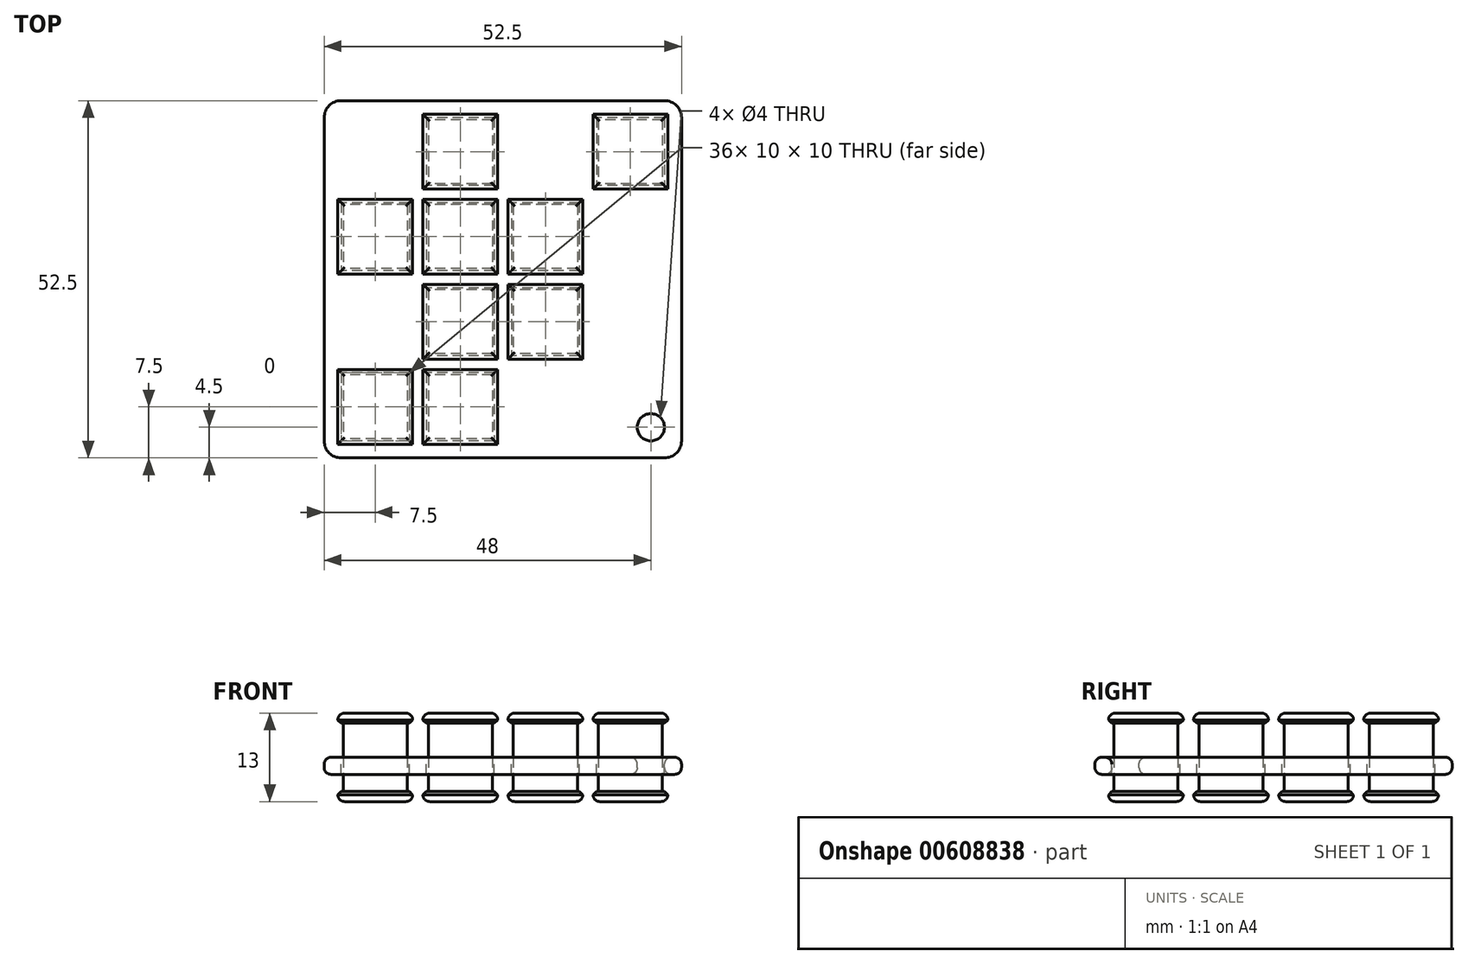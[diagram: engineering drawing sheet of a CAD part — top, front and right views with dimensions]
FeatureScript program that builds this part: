
annotation { "Feature Type Name" : "Feature", "Feature Type Description" : "" }
export const myFeature = defineFeature(function(context is Context, id is Id, definition is map)
    precondition{}
    {
        {
            var Q0;
            Q0=qCreatedBy(makeId("Top.planeOp"),FACE);
            var sketch = newSketch(context, id + "F0", { "sketchPlane" : qUnion([Q0])});
            skLineSegment(sketch, "E0.bottom", {"start": v(5, 5) * mm, "end": v(-5, 5) * mm});
            skLineSegment(sketch, "E0.top", {"start": v(5, -5) * mm, "end": v(-5, -5) * mm});
            skLineSegment(sketch, "E0.left", {"start": v(5, 5) * mm, "end": v(5, -5) * mm});
            skLineSegment(sketch, "E0.right", {"start": v(-5, 5) * mm, "end": v(-5, -5) * mm});
            skPoint(sketch, "E0.middle", {"position": v(0, 0) * mm});
            skLineSegment(sketch, "E1.0.2.0", {"start": v(5, 30) * mm, "end": v(-5, 30) * mm});
            skLineSegment(sketch, "E1.0.2.1", {"start": v(5, 30) * mm, "end": v(5, 20) * mm});
            skLineSegment(sketch, "E1.0.2.2", {"start": v(5, 20) * mm, "end": v(-5, 20) * mm});
            skLineSegment(sketch, "E1.0.2.3", {"start": v(-5, 30) * mm, "end": v(-5, 20) * mm});
            skLineSegment(sketch, "E1.1.0.0", {"start": v(17.5, 5) * mm, "end": v(7.5, 5) * mm});
            skLineSegment(sketch, "E1.1.0.1", {"start": v(17.5, 5) * mm, "end": v(17.5, -5) * mm});
            skLineSegment(sketch, "E1.1.0.2", {"start": v(17.5, -5) * mm, "end": v(7.5, -5) * mm});
            skLineSegment(sketch, "E1.1.0.3", {"start": v(7.5, 5) * mm, "end": v(7.5, -5) * mm});
            skLineSegment(sketch, "E1.1.1.0", {"start": v(17.5, 17.5) * mm, "end": v(7.5, 17.5) * mm});
            skLineSegment(sketch, "E1.1.1.1", {"start": v(17.5, 17.5) * mm, "end": v(17.5, 7.5) * mm});
            skLineSegment(sketch, "E1.1.1.2", {"start": v(17.5, 7.5) * mm, "end": v(7.5, 7.5) * mm});
            skLineSegment(sketch, "E1.1.1.3", {"start": v(7.5, 17.5) * mm, "end": v(7.5, 7.5) * mm});
            skLineSegment(sketch, "E1.1.2.0", {"start": v(17.5, 30) * mm, "end": v(7.5, 30) * mm});
            skLineSegment(sketch, "E1.1.2.1", {"start": v(17.5, 30) * mm, "end": v(17.5, 20) * mm});
            skLineSegment(sketch, "E1.1.2.2", {"start": v(17.5, 20) * mm, "end": v(7.5, 20) * mm});
            skLineSegment(sketch, "E1.1.2.3", {"start": v(7.5, 30) * mm, "end": v(7.5, 20) * mm});
            skLineSegment(sketch, "E1.1.3.0", {"start": v(17.5, 42.5) * mm, "end": v(7.5, 42.5) * mm});
            skLineSegment(sketch, "E1.1.3.1", {"start": v(17.5, 42.5) * mm, "end": v(17.5, 32.5) * mm});
            skLineSegment(sketch, "E1.1.3.2", {"start": v(17.5, 32.5) * mm, "end": v(7.5, 32.5) * mm});
            skLineSegment(sketch, "E1.1.3.3", {"start": v(7.5, 42.5) * mm, "end": v(7.5, 32.5) * mm});
            skLineSegment(sketch, "E1.2.1.0", {"start": v(30, 17.5) * mm, "end": v(20, 17.5) * mm});
            skLineSegment(sketch, "E1.2.1.1", {"start": v(30, 17.5) * mm, "end": v(30, 7.5) * mm});
            skLineSegment(sketch, "E1.2.1.2", {"start": v(30, 7.5) * mm, "end": v(20, 7.5) * mm});
            skLineSegment(sketch, "E1.2.1.3", {"start": v(20, 17.5) * mm, "end": v(20, 7.5) * mm});
            skLineSegment(sketch, "E1.2.2.0", {"start": v(30, 30) * mm, "end": v(20, 30) * mm});
            skLineSegment(sketch, "E1.2.2.1", {"start": v(30, 30) * mm, "end": v(30, 20) * mm});
            skLineSegment(sketch, "E1.2.2.2", {"start": v(30, 20) * mm, "end": v(20, 20) * mm});
            skLineSegment(sketch, "E1.2.2.3", {"start": v(20, 30) * mm, "end": v(20, 20) * mm});
            skLineSegment(sketch, "E1.3.3.0", {"start": v(42.5, 42.5) * mm, "end": v(32.5, 42.5) * mm});
            skLineSegment(sketch, "E1.3.3.1", {"start": v(42.5, 42.5) * mm, "end": v(42.5, 32.5) * mm});
            skLineSegment(sketch, "E1.3.3.2", {"start": v(42.5, 32.5) * mm, "end": v(32.5, 32.5) * mm});
            skLineSegment(sketch, "E1.3.3.3", {"start": v(32.5, 42.5) * mm, "end": v(32.5, 32.5) * mm});
            skLineSegment(sketch, "E2.bottom", {"start": v(-5, -7.5) * mm, "end": v(42.5, -7.5) * mm});
            skLineSegment(sketch, "E2.top", {"start": v(-5, 45) * mm, "end": v(42.5, 45) * mm});
            skLineSegment(sketch, "E2.left", {"start": v(-7.5, -5) * mm, "end": v(-7.5, 42.5) * mm});
            skLineSegment(sketch, "E2.right", {"start": v(45, -5) * mm, "end": v(45, 42.5) * mm});
            skPoint(sketch, "E3.visualSharp", {"position": v(-7.5, 45) * mm});
            skArc(sketch, "E3.filletArc", {"start": v(-5, 45) * mm, "mid": v(-6.77, 44.27) * mm, "end": v(-7.5, 42.5) * mm});
            skPoint(sketch, "E4.visualSharp", {"position": v(-7.5, -7.5) * mm});
            skArc(sketch, "E4.filletArc", {"start": v(-7.5, -5) * mm, "mid": v(-6.77, -6.77) * mm, "end": v(-5, -7.5) * mm});
            skPoint(sketch, "E5.visualSharp", {"position": v(45, -7.5) * mm});
            skArc(sketch, "E5.filletArc", {"start": v(42.5, -7.5) * mm, "mid": v(44.27, -6.77) * mm, "end": v(45, -5) * mm});
            skPoint(sketch, "E6.visualSharp", {"position": v(45, 45) * mm});
            skArc(sketch, "E6.filletArc", {"start": v(45, 42.5) * mm, "mid": v(44.27, 44.27) * mm, "end": v(42.5, 45) * mm});
            skLineSegment(sketch, "E7.0", {"start": v(4.7, 4.7) * mm, "end": v(-4.7, 4.7) * mm});
            skLineSegment(sketch, "E7.1", {"start": v(4.7, 4.7) * mm, "end": v(4.7, -4.7) * mm});
            skLineSegment(sketch, "E7.2", {"start": v(4.7, -4.7) * mm, "end": v(-4.7, -4.7) * mm});
            skLineSegment(sketch, "E7.3", {"start": v(-4.7, 4.7) * mm, "end": v(-4.7, -4.7) * mm});
            skLineSegment(sketch, "E8.0.2.0", {"start": v(4.7, 29.7) * mm, "end": v(-4.7, 29.7) * mm});
            skLineSegment(sketch, "E8.0.2.1", {"start": v(4.7, 29.7) * mm, "end": v(4.7, 20.3) * mm});
            skLineSegment(sketch, "E8.0.2.2", {"start": v(4.7, 20.3) * mm, "end": v(-4.7, 20.3) * mm});
            skLineSegment(sketch, "E8.0.2.3", {"start": v(-4.7, 29.7) * mm, "end": v(-4.7, 20.3) * mm});
            skLineSegment(sketch, "E8.1.0.0", {"start": v(17.2, 4.7) * mm, "end": v(7.8, 4.7) * mm});
            skLineSegment(sketch, "E8.1.0.1", {"start": v(17.2, 4.7) * mm, "end": v(17.2, -4.7) * mm});
            skLineSegment(sketch, "E8.1.0.2", {"start": v(17.2, -4.7) * mm, "end": v(7.8, -4.7) * mm});
            skLineSegment(sketch, "E8.1.0.3", {"start": v(7.8, 4.7) * mm, "end": v(7.8, -4.7) * mm});
            skLineSegment(sketch, "E8.1.1.0", {"start": v(17.2, 17.2) * mm, "end": v(7.8, 17.2) * mm});
            skLineSegment(sketch, "E8.1.1.1", {"start": v(17.2, 17.2) * mm, "end": v(17.2, 7.8) * mm});
            skLineSegment(sketch, "E8.1.1.2", {"start": v(17.2, 7.8) * mm, "end": v(7.8, 7.8) * mm});
            skLineSegment(sketch, "E8.1.1.3", {"start": v(7.8, 17.2) * mm, "end": v(7.8, 7.8) * mm});
            skLineSegment(sketch, "E8.1.2.0", {"start": v(17.2, 29.7) * mm, "end": v(7.8, 29.7) * mm});
            skLineSegment(sketch, "E8.1.2.1", {"start": v(17.2, 29.7) * mm, "end": v(17.2, 20.3) * mm});
            skLineSegment(sketch, "E8.1.2.2", {"start": v(17.2, 20.3) * mm, "end": v(7.8, 20.3) * mm});
            skLineSegment(sketch, "E8.1.2.3", {"start": v(7.8, 29.7) * mm, "end": v(7.8, 20.3) * mm});
            skLineSegment(sketch, "E8.1.3.0", {"start": v(17.2, 42.2) * mm, "end": v(7.8, 42.2) * mm});
            skLineSegment(sketch, "E8.1.3.1", {"start": v(17.2, 42.2) * mm, "end": v(17.2, 32.8) * mm});
            skLineSegment(sketch, "E8.1.3.2", {"start": v(17.2, 32.8) * mm, "end": v(7.8, 32.8) * mm});
            skLineSegment(sketch, "E8.1.3.3", {"start": v(7.8, 42.2) * mm, "end": v(7.8, 32.8) * mm});
            skLineSegment(sketch, "E8.2.1.0", {"start": v(29.7, 17.2) * mm, "end": v(20.3, 17.2) * mm});
            skLineSegment(sketch, "E8.2.1.1", {"start": v(29.7, 17.2) * mm, "end": v(29.7, 7.8) * mm});
            skLineSegment(sketch, "E8.2.1.2", {"start": v(29.7, 7.8) * mm, "end": v(20.3, 7.8) * mm});
            skLineSegment(sketch, "E8.2.1.3", {"start": v(20.3, 17.2) * mm, "end": v(20.3, 7.8) * mm});
            skLineSegment(sketch, "E8.2.2.0", {"start": v(29.7, 29.7) * mm, "end": v(20.3, 29.7) * mm});
            skLineSegment(sketch, "E8.2.2.1", {"start": v(29.7, 29.7) * mm, "end": v(29.7, 20.3) * mm});
            skLineSegment(sketch, "E8.2.2.2", {"start": v(29.7, 20.3) * mm, "end": v(20.3, 20.3) * mm});
            skLineSegment(sketch, "E8.2.2.3", {"start": v(20.3, 29.7) * mm, "end": v(20.3, 20.3) * mm});
            skLineSegment(sketch, "E8.3.3.0", {"start": v(42.2, 42.2) * mm, "end": v(32.8, 42.2) * mm});
            skLineSegment(sketch, "E8.3.3.1", {"start": v(42.2, 42.2) * mm, "end": v(42.2, 32.8) * mm});
            skLineSegment(sketch, "E8.3.3.2", {"start": v(42.2, 32.8) * mm, "end": v(32.8, 32.8) * mm});
            skLineSegment(sketch, "E8.3.3.3", {"start": v(32.8, 42.2) * mm, "end": v(32.8, 32.8) * mm});
            skLineSegment(sketch, "E8.direction1", {"start": v(-4.7, 4.7) * mm, "end": v(7.8, 4.7) * mm, "construction": true});
            skCircle(sketch, "E9", {"center": v(40.5, -3) * mm, "radius": 2 * mm});
            skSolve(sketch);
        }
        {
            var Q0;
            Q0=makeQuery(id+"F0.imprint","IMPRINT",FACE,{"disambiguationData":[TD([[makeQuery(id+"F0.imprint","IMPRINT",EDGE,{"derivedFrom":sQuery(id+"F0.wireOp",EDGE,"E7.0")}),1.0]])]});
            var Q1;
            Q1=makeQuery(id+"F0.imprint","IMPRINT",FACE,{"disambiguationData":[TD([[makeQuery(id+"F0.imprint","IMPRINT",EDGE,{"derivedFrom":sQuery(id+"F0.wireOp",EDGE,"E8.1.0.0")}),1.0]])]});
            var Q2;
            Q2=makeQuery(id+"F0.imprint","IMPRINT",FACE,{"disambiguationData":[TD([[makeQuery(id+"F0.imprint","IMPRINT",EDGE,{"derivedFrom":sQuery(id+"F0.wireOp",EDGE,"E8.1.1.0")}),1.0]])]});
            var Q3;
            Q3=makeQuery(id+"F0.imprint","IMPRINT",FACE,{"disambiguationData":[TD([[makeQuery(id+"F0.imprint","IMPRINT",EDGE,{"derivedFrom":sQuery(id+"F0.wireOp",EDGE,"E8.2.1.0")}),1.0]])]});
            var Q4;
            Q4=makeQuery(id+"F0.imprint","IMPRINT",FACE,{"disambiguationData":[TD([[makeQuery(id+"F0.imprint","IMPRINT",EDGE,{"derivedFrom":sQuery(id+"F0.wireOp",EDGE,"E8.2.2.0")}),1.0]])]});
            var Q5;
            Q5=makeQuery(id+"F0.imprint","IMPRINT",FACE,{"disambiguationData":[TD([[makeQuery(id+"F0.imprint","IMPRINT",EDGE,{"derivedFrom":sQuery(id+"F0.wireOp",EDGE,"E8.1.2.0")}),1.0]])]});
            var Q6;
            Q6=makeQuery(id+"F0.imprint","IMPRINT",FACE,{"disambiguationData":[TD([[makeQuery(id+"F0.imprint","IMPRINT",EDGE,{"derivedFrom":sQuery(id+"F0.wireOp",EDGE,"E8.0.2.0")}),1.0]])]});
            var Q7;
            Q7=makeQuery(id+"F0.imprint","IMPRINT",FACE,{"disambiguationData":[TD([[makeQuery(id+"F0.imprint","IMPRINT",EDGE,{"derivedFrom":sQuery(id+"F0.wireOp",EDGE,"E8.3.3.0")}),1.0]])]});
            var Q8;
            Q8=makeQuery(id+"F0.imprint","IMPRINT",FACE,{"disambiguationData":[TD([[makeQuery(id+"F0.imprint","IMPRINT",EDGE,{"derivedFrom":sQuery(id+"F0.wireOp",EDGE,"E8.1.3.0")}),1.0]])]});
            extrude(context, id + "F1", {"entities" : qUnion([Q0, Q1, Q2, Q3, Q4, Q5, Q6, Q7, Q8]), "endBound" : BoundingType.SYMMETRIC, "depth" : 10 * mm, "offsetDistance" : 25 * mm});
        }
        {
            var Q0;
            Q0=makeQuery(id+"F0.imprint","IMPRINT",FACE,{"disambiguationData":[TD([[makeQuery(id+"F0.imprint","IMPRINT",EDGE,{"derivedFrom":sQuery(id+"F0.wireOp",EDGE,"E0.bottom")}),-1.0]])]});
            extrude(context, id + "F2", {"entities" : qUnion([Q0]), "oppositeDirection" : true, "depth" : 2.5 * mm, "offsetDistance" : 25 * mm});
        }
        {
            var Q0;
            Q0=makeQuery(id+"F1.opExtrude","CAP_FACE",FACE,{"disambiguationData":[OSD([sQuery(id+"F0.wireOp",EDGE,"E7.0"),sQuery(id+"F0.wireOp",EDGE,"E7.1"),sQuery(id+"F0.wireOp",EDGE,"E7.2"),sQuery(id+"F0.wireOp",EDGE,"E7.3")])],"isStart":false});
            var sketch = newSketch(context, id + "F3", { "sketchPlane" : qUnion([Q0])});
            skLineSegment(sketch, "E10.0", {"start": v(5.5, 5.5) * mm, "end": v(-5.5, 5.5) * mm});
            skLineSegment(sketch, "E10.1", {"start": v(5.5, 5.5) * mm, "end": v(5.5, -5.5) * mm});
            skLineSegment(sketch, "E10.2", {"start": v(5.5, -5.5) * mm, "end": v(-5.5, -5.5) * mm});
            skLineSegment(sketch, "E10.3", {"start": v(-5.5, 5.5) * mm, "end": v(-5.5, -5.5) * mm});
            skLineSegment(sketch, "E11.0.1.0", {"start": v(5.5, 18) * mm, "end": v(-5.5, 18) * mm});
            skLineSegment(sketch, "E11.0.1.1", {"start": v(5.5, 18) * mm, "end": v(5.5, 7) * mm});
            skLineSegment(sketch, "E11.0.1.2", {"start": v(5.5, 7) * mm, "end": v(-5.5, 7) * mm});
            skLineSegment(sketch, "E11.0.1.3", {"start": v(-5.5, 18) * mm, "end": v(-5.5, 7) * mm});
            skLineSegment(sketch, "E11.0.2.0", {"start": v(5.5, 30.5) * mm, "end": v(-5.5, 30.5) * mm});
            skLineSegment(sketch, "E11.0.2.1", {"start": v(5.5, 30.5) * mm, "end": v(5.5, 19.5) * mm});
            skLineSegment(sketch, "E11.0.2.2", {"start": v(5.5, 19.5) * mm, "end": v(-5.5, 19.5) * mm});
            skLineSegment(sketch, "E11.0.2.3", {"start": v(-5.5, 30.5) * mm, "end": v(-5.5, 19.5) * mm});
            skLineSegment(sketch, "E11.0.3.0", {"start": v(5.5, 43) * mm, "end": v(-5.5, 43) * mm});
            skLineSegment(sketch, "E11.0.3.1", {"start": v(5.5, 43) * mm, "end": v(5.5, 32) * mm});
            skLineSegment(sketch, "E11.0.3.2", {"start": v(5.5, 32) * mm, "end": v(-5.5, 32) * mm});
            skLineSegment(sketch, "E11.0.3.3", {"start": v(-5.5, 43) * mm, "end": v(-5.5, 32) * mm});
            skLineSegment(sketch, "E11.1.0.0", {"start": v(18, 5.5) * mm, "end": v(7, 5.5) * mm});
            skLineSegment(sketch, "E11.1.0.1", {"start": v(18, 5.5) * mm, "end": v(18, -5.5) * mm});
            skLineSegment(sketch, "E11.1.0.2", {"start": v(18, -5.5) * mm, "end": v(7, -5.5) * mm});
            skLineSegment(sketch, "E11.1.0.3", {"start": v(7, 5.5) * mm, "end": v(7, -5.5) * mm});
            skLineSegment(sketch, "E11.1.1.0", {"start": v(18, 18) * mm, "end": v(7, 18) * mm});
            skLineSegment(sketch, "E11.1.1.1", {"start": v(18, 18) * mm, "end": v(18, 7) * mm});
            skLineSegment(sketch, "E11.1.1.2", {"start": v(18, 7) * mm, "end": v(7, 7) * mm});
            skLineSegment(sketch, "E11.1.1.3", {"start": v(7, 18) * mm, "end": v(7, 7) * mm});
            skLineSegment(sketch, "E11.1.2.0", {"start": v(18, 30.5) * mm, "end": v(7, 30.5) * mm});
            skLineSegment(sketch, "E11.1.2.1", {"start": v(18, 30.5) * mm, "end": v(18, 19.5) * mm});
            skLineSegment(sketch, "E11.1.2.2", {"start": v(18, 19.5) * mm, "end": v(7, 19.5) * mm});
            skLineSegment(sketch, "E11.1.2.3", {"start": v(7, 30.5) * mm, "end": v(7, 19.5) * mm});
            skLineSegment(sketch, "E11.1.3.0", {"start": v(18, 43) * mm, "end": v(7, 43) * mm});
            skLineSegment(sketch, "E11.1.3.1", {"start": v(18, 43) * mm, "end": v(18, 32) * mm});
            skLineSegment(sketch, "E11.1.3.2", {"start": v(18, 32) * mm, "end": v(7, 32) * mm});
            skLineSegment(sketch, "E11.1.3.3", {"start": v(7, 43) * mm, "end": v(7, 32) * mm});
            skLineSegment(sketch, "E11.2.0.0", {"start": v(30.5, 5.5) * mm, "end": v(19.5, 5.5) * mm});
            skLineSegment(sketch, "E11.2.0.1", {"start": v(30.5, 5.5) * mm, "end": v(30.5, -5.5) * mm});
            skLineSegment(sketch, "E11.2.0.2", {"start": v(30.5, -5.5) * mm, "end": v(19.5, -5.5) * mm});
            skLineSegment(sketch, "E11.2.0.3", {"start": v(19.5, 5.5) * mm, "end": v(19.5, -5.5) * mm});
            skLineSegment(sketch, "E11.2.1.0", {"start": v(30.5, 18) * mm, "end": v(19.5, 18) * mm});
            skLineSegment(sketch, "E11.2.1.1", {"start": v(30.5, 18) * mm, "end": v(30.5, 7) * mm});
            skLineSegment(sketch, "E11.2.1.2", {"start": v(30.5, 7) * mm, "end": v(19.5, 7) * mm});
            skLineSegment(sketch, "E11.2.1.3", {"start": v(19.5, 18) * mm, "end": v(19.5, 7) * mm});
            skLineSegment(sketch, "E11.2.2.0", {"start": v(30.5, 30.5) * mm, "end": v(19.5, 30.5) * mm});
            skLineSegment(sketch, "E11.2.2.1", {"start": v(30.5, 30.5) * mm, "end": v(30.5, 19.5) * mm});
            skLineSegment(sketch, "E11.2.2.2", {"start": v(30.5, 19.5) * mm, "end": v(19.5, 19.5) * mm});
            skLineSegment(sketch, "E11.2.2.3", {"start": v(19.5, 30.5) * mm, "end": v(19.5, 19.5) * mm});
            skLineSegment(sketch, "E11.2.3.0", {"start": v(30.5, 43) * mm, "end": v(19.5, 43) * mm});
            skLineSegment(sketch, "E11.2.3.1", {"start": v(30.5, 43) * mm, "end": v(30.5, 32) * mm});
            skLineSegment(sketch, "E11.2.3.2", {"start": v(30.5, 32) * mm, "end": v(19.5, 32) * mm});
            skLineSegment(sketch, "E11.2.3.3", {"start": v(19.5, 43) * mm, "end": v(19.5, 32) * mm});
            skLineSegment(sketch, "E11.3.0.0", {"start": v(43, 5.5) * mm, "end": v(32, 5.5) * mm});
            skLineSegment(sketch, "E11.3.0.1", {"start": v(43, 5.5) * mm, "end": v(43, -5.5) * mm});
            skLineSegment(sketch, "E11.3.0.2", {"start": v(43, -5.5) * mm, "end": v(32, -5.5) * mm});
            skLineSegment(sketch, "E11.3.0.3", {"start": v(32, 5.5) * mm, "end": v(32, -5.5) * mm});
            skLineSegment(sketch, "E11.3.1.0", {"start": v(43, 18) * mm, "end": v(32, 18) * mm});
            skLineSegment(sketch, "E11.3.1.1", {"start": v(43, 18) * mm, "end": v(43, 7) * mm});
            skLineSegment(sketch, "E11.3.1.2", {"start": v(43, 7) * mm, "end": v(32, 7) * mm});
            skLineSegment(sketch, "E11.3.1.3", {"start": v(32, 18) * mm, "end": v(32, 7) * mm});
            skLineSegment(sketch, "E11.3.2.0", {"start": v(43, 30.5) * mm, "end": v(32, 30.5) * mm});
            skLineSegment(sketch, "E11.3.2.1", {"start": v(43, 30.5) * mm, "end": v(43, 19.5) * mm});
            skLineSegment(sketch, "E11.3.2.2", {"start": v(43, 19.5) * mm, "end": v(32, 19.5) * mm});
            skLineSegment(sketch, "E11.3.2.3", {"start": v(32, 30.5) * mm, "end": v(32, 19.5) * mm});
            skLineSegment(sketch, "E11.3.3.0", {"start": v(43, 43) * mm, "end": v(32, 43) * mm});
            skLineSegment(sketch, "E11.3.3.1", {"start": v(43, 43) * mm, "end": v(43, 32) * mm});
            skLineSegment(sketch, "E11.3.3.2", {"start": v(43, 32) * mm, "end": v(32, 32) * mm});
            skLineSegment(sketch, "E11.3.3.3", {"start": v(32, 43) * mm, "end": v(32, 32) * mm});
            skLineSegment(sketch, "E11.direction1", {"start": v(-5.5, 5.5) * mm, "end": v(7, 5.5) * mm, "construction": true});
            skLineSegment(sketch, "E11.direction2", {"start": v(-5.5, 5.5) * mm, "end": v(-5.5, 18) * mm, "construction": true});
            skSolve(sketch);
        }
        {
            var Q0;
            Q0=makeQuery(id+"F3.imprint","IMPRINT",FACE,{"disambiguationData":[TD([[makeQuery(id+"F3.imprint","IMPRINT",EDGE,{"derivedFrom":sQuery(id+"F3.wireOp",EDGE,"E11.0.2.0")}),1.0]])]});
            var Q1;
            Q1=makeQuery(id+"F3.imprint","IMPRINT",FACE,{"disambiguationData":[TD([[makeQuery(id+"F3.imprint","IMPRINT",EDGE,{"derivedFrom":sQuery(id+"F3.wireOp",EDGE,"E11.1.0.0")}),1.0]])]});
            var Q2;
            Q2=makeQuery(id+"F3.imprint","IMPRINT",FACE,{"disambiguationData":[TD([[makeQuery(id+"F3.imprint","IMPRINT",EDGE,{"derivedFrom":sQuery(id+"F3.wireOp",EDGE,"E11.1.1.0")}),1.0]])]});
            var Q3;
            Q3=makeQuery(id+"F3.imprint","IMPRINT",FACE,{"disambiguationData":[TD([[makeQuery(id+"F3.imprint","IMPRINT",EDGE,{"derivedFrom":sQuery(id+"F3.wireOp",EDGE,"E11.1.2.0")}),1.0]])]});
            var Q4;
            Q4=makeQuery(id+"F3.imprint","IMPRINT",FACE,{"disambiguationData":[TD([[makeQuery(id+"F3.imprint","IMPRINT",EDGE,{"derivedFrom":sQuery(id+"F3.wireOp",EDGE,"E11.1.3.0")}),1.0]])]});
            var Q5;
            Q5=makeQuery(id+"F3.imprint","IMPRINT",FACE,{"disambiguationData":[TD([[makeQuery(id+"F3.imprint","IMPRINT",EDGE,{"derivedFrom":sQuery(id+"F3.wireOp",EDGE,"E11.3.3.0")}),1.0]])]});
            var Q6;
            Q6=makeQuery(id+"F3.imprint","IMPRINT",FACE,{"disambiguationData":[TD([[makeQuery(id+"F3.imprint","IMPRINT",EDGE,{"derivedFrom":sQuery(id+"F3.wireOp",EDGE,"E11.2.2.0")}),1.0]])]});
            var Q7;
            Q7=makeQuery(id+"F3.imprint","IMPRINT",FACE,{"disambiguationData":[TD([[makeQuery(id+"F3.imprint","IMPRINT",EDGE,{"derivedFrom":sQuery(id+"F3.wireOp",EDGE,"E11.2.1.0")}),1.0]])]});
            var Q8;
            Q8=makeQuery(id+"F3.imprint","IMPRINT",FACE,{"disambiguationData":[TD([[makeQuery(id+"F3.imprint","IMPRINT",EDGE,{"derivedFrom":sQuery(id+"F3.wireOp",EDGE,"E10.0")}),1.0]])]});
            var Q9;
            Q9=makeQuery(id+"F3.imprint","IMPRINT",FACE,{"disambiguationData":[TD([[makeQuery(id+"F3.imprint","IMPRINT",EDGE,{"derivedFrom":makeQuery(id+"F1.opExtrude","CAP_EDGE",EDGE,{"disambiguationData":[OSD([sQuery(id+"F0.wireOp",EDGE,"E7.0")])],"isStart":false})}),1.0]])]});
            extrude(context, id + "F4", {"entities" : qUnion([Q0, Q1, Q2, Q3, Q4, Q5, Q6, Q7, Q8, Q9]), "depth" : 1.5 * mm, "offsetDistance" : 25 * mm});
        }
        {
            var Q0;
            Q0=makeQuery(id+"F4.opExtrude","SWEPT_BODY",BODY,{"disambiguationData":[OSD([sQuery(id+"F0.wireOp",EDGE,"E7.0"),sQuery(id+"F0.wireOp",EDGE,"E7.1"),sQuery(id+"F0.wireOp",EDGE,"E7.2"),sQuery(id+"F0.wireOp",EDGE,"E7.3")])]});
            var Q1;
            Q1=makeQuery(id+"F4.opExtrude","SWEPT_BODY",BODY,{"disambiguationData":[OSD([sQuery(id+"F3.wireOp",EDGE,"E11.1.0.0"),sQuery(id+"F3.wireOp",EDGE,"E11.1.0.1"),sQuery(id+"F3.wireOp",EDGE,"E11.1.0.2"),sQuery(id+"F3.wireOp",EDGE,"E11.1.0.3")])]});
            var Q2;
            Q2=makeQuery(id+"F4.opExtrude","SWEPT_BODY",BODY,{"disambiguationData":[OSD([sQuery(id+"F3.wireOp",EDGE,"E11.2.1.0"),sQuery(id+"F3.wireOp",EDGE,"E11.2.1.1"),sQuery(id+"F3.wireOp",EDGE,"E11.2.1.2"),sQuery(id+"F3.wireOp",EDGE,"E11.2.1.3")])]});
            var Q3;
            Q3=makeQuery(id+"F4.opExtrude","SWEPT_BODY",BODY,{"disambiguationData":[OSD([sQuery(id+"F3.wireOp",EDGE,"E11.2.2.0"),sQuery(id+"F3.wireOp",EDGE,"E11.2.2.1"),sQuery(id+"F3.wireOp",EDGE,"E11.2.2.2"),sQuery(id+"F3.wireOp",EDGE,"E11.2.2.3")])]});
            var Q4;
            Q4=makeQuery(id+"F4.opExtrude","SWEPT_BODY",BODY,{"disambiguationData":[OSD([sQuery(id+"F3.wireOp",EDGE,"E11.3.3.0"),sQuery(id+"F3.wireOp",EDGE,"E11.3.3.1"),sQuery(id+"F3.wireOp",EDGE,"E11.3.3.2"),sQuery(id+"F3.wireOp",EDGE,"E11.3.3.3")])]});
            var Q5;
            Q5=makeQuery(id+"F4.opExtrude","SWEPT_BODY",BODY,{"disambiguationData":[OSD([sQuery(id+"F3.wireOp",EDGE,"E11.1.3.0"),sQuery(id+"F3.wireOp",EDGE,"E11.1.3.1"),sQuery(id+"F3.wireOp",EDGE,"E11.1.3.2"),sQuery(id+"F3.wireOp",EDGE,"E11.1.3.3")])]});
            var Q6;
            Q6=makeQuery(id+"F4.opExtrude","SWEPT_BODY",BODY,{"disambiguationData":[OSD([sQuery(id+"F3.wireOp",EDGE,"E11.1.2.0"),sQuery(id+"F3.wireOp",EDGE,"E11.1.2.1"),sQuery(id+"F3.wireOp",EDGE,"E11.1.2.2"),sQuery(id+"F3.wireOp",EDGE,"E11.1.2.3")])]});
            var Q7;
            Q7=makeQuery(id+"F4.opExtrude","SWEPT_BODY",BODY,{"disambiguationData":[OSD([sQuery(id+"F3.wireOp",EDGE,"E11.1.1.0"),sQuery(id+"F3.wireOp",EDGE,"E11.1.1.1"),sQuery(id+"F3.wireOp",EDGE,"E11.1.1.2"),sQuery(id+"F3.wireOp",EDGE,"E11.1.1.3")])]});
            var Q8;
            Q8=makeQuery(id+"F4.opExtrude","SWEPT_BODY",BODY,{"disambiguationData":[OSD([sQuery(id+"F3.wireOp",EDGE,"E10.0"),sQuery(id+"F3.wireOp",EDGE,"E10.1"),sQuery(id+"F3.wireOp",EDGE,"E10.2"),sQuery(id+"F3.wireOp",EDGE,"E10.3")])]});
            var Q9;
            Q9=makeQuery(id+"F4.opExtrude","SWEPT_BODY",BODY,{"disambiguationData":[OSD([sQuery(id+"F3.wireOp",EDGE,"E11.0.2.0"),sQuery(id+"F3.wireOp",EDGE,"E11.0.2.1"),sQuery(id+"F3.wireOp",EDGE,"E11.0.2.2"),sQuery(id+"F3.wireOp",EDGE,"E11.0.2.3")])]});
            var Q10;
            Q10=qCreatedBy(makeId("Top.planeOp"),FACE);
            mirror(context, id + "F5", {"entities" : qUnion([Q0, Q1, Q2, Q3, Q4, Q5, Q6, Q7, Q8, Q9]), "mirrorPlane" : qUnion([Q10])});
        }
        {
            var Q0;
            Q0=makeQuery(id+"F4.opExtrude","CAP_EDGE",EDGE,{"disambiguationData":[OSD([sQuery(id+"F3.wireOp",EDGE,"E11.3.3.0")])],"isStart":true});
            var Q1;
            Q1=makeQuery(id+"F4.opExtrude","CAP_EDGE",EDGE,{"disambiguationData":[OSD([sQuery(id+"F3.wireOp",EDGE,"E11.1.3.0")])],"isStart":true});
            var Q2;
            Q2=makeQuery(id+"F4.opExtrude","CAP_EDGE",EDGE,{"disambiguationData":[OSD([sQuery(id+"F3.wireOp",EDGE,"E11.3.3.3")])],"isStart":true});
            var Q3;
            Q3=makeQuery(id+"F4.opExtrude","CAP_EDGE",EDGE,{"disambiguationData":[OSD([sQuery(id+"F3.wireOp",EDGE,"E11.1.3.3")])],"isStart":true});
            var Q4;
            Q4=makeQuery(id+"F4.opExtrude","CAP_EDGE",EDGE,{"disambiguationData":[OSD([sQuery(id+"F3.wireOp",EDGE,"E11.1.2.0")])],"isStart":true});
            var Q5;
            Q5=makeQuery(id+"F4.opExtrude","CAP_EDGE",EDGE,{"disambiguationData":[OSD([sQuery(id+"F3.wireOp",EDGE,"E11.1.2.3")])],"isStart":true});
            var Q6;
            Q6=makeQuery(id+"F4.opExtrude","CAP_EDGE",EDGE,{"disambiguationData":[OSD([sQuery(id+"F3.wireOp",EDGE,"E11.0.2.0")])],"isStart":true});
            var Q7;
            Q7=makeQuery(id+"F4.opExtrude","CAP_EDGE",EDGE,{"disambiguationData":[OSD([sQuery(id+"F3.wireOp",EDGE,"E11.0.2.3")])],"isStart":true});
            var Q8;
            Q8=makeQuery(id+"F4.opExtrude","CAP_EDGE",EDGE,{"disambiguationData":[OSD([sQuery(id+"F3.wireOp",EDGE,"E11.1.1.3")])],"isStart":true});
            var Q9;
            Q9=makeQuery(id+"F4.opExtrude","CAP_EDGE",EDGE,{"disambiguationData":[OSD([sQuery(id+"F3.wireOp",EDGE,"E11.1.0.0")])],"isStart":true});
            var Q10;
            Q10=makeQuery(id+"F4.opExtrude","CAP_EDGE",EDGE,{"disambiguationData":[OSD([sQuery(id+"F3.wireOp",EDGE,"E10.0")])],"isStart":true});
            var Q11;
            Q11=makeQuery(id+"F4.opExtrude","CAP_EDGE",EDGE,{"disambiguationData":[OSD([sQuery(id+"F3.wireOp",EDGE,"E10.3")])],"isStart":true});
            var Q12;
            Q12=makeQuery(id+"F4.opExtrude","CAP_EDGE",EDGE,{"disambiguationData":[OSD([sQuery(id+"F3.wireOp",EDGE,"E11.1.0.3")])],"isStart":true});
            var Q13;
            Q13=makeQuery(id+"F4.opExtrude","CAP_EDGE",EDGE,{"disambiguationData":[OSD([sQuery(id+"F3.wireOp",EDGE,"E11.1.1.0")])],"isStart":true});
            var Q14;
            Q14=makeQuery(id+"F4.opExtrude","CAP_EDGE",EDGE,{"disambiguationData":[OSD([sQuery(id+"F3.wireOp",EDGE,"E11.2.1.0")])],"isStart":true});
            var Q15;
            Q15=makeQuery(id+"F4.opExtrude","CAP_EDGE",EDGE,{"disambiguationData":[OSD([sQuery(id+"F3.wireOp",EDGE,"E11.2.2.0")])],"isStart":true});
            var Q16;
            Q16=makeQuery(id+"F4.opExtrude","CAP_EDGE",EDGE,{"disambiguationData":[OSD([sQuery(id+"F3.wireOp",EDGE,"E11.2.2.3")])],"isStart":true});
            var Q17;
            Q17=makeQuery(id+"F4.opExtrude","CAP_EDGE",EDGE,{"disambiguationData":[OSD([sQuery(id+"F3.wireOp",EDGE,"E11.2.1.3")])],"isStart":true});
            var Q18;
            Q18=makeQuery(id+"F5.opPattern","COPY",EDGE,{"derivedFrom":makeQuery(id+"F4.opExtrude","CAP_EDGE",EDGE,{"disambiguationData":[OSD([sQuery(id+"F3.wireOp",EDGE,"E11.3.3.0")])],"isStart":true}),"instanceName":"1"});
            var Q19;
            Q19=makeQuery(id+"F5.opPattern","COPY",EDGE,{"derivedFrom":makeQuery(id+"F4.opExtrude","CAP_EDGE",EDGE,{"disambiguationData":[OSD([sQuery(id+"F3.wireOp",EDGE,"E11.3.3.3")])],"isStart":true}),"instanceName":"1"});
            var Q20;
            Q20=makeQuery(id+"F5.opPattern","COPY",EDGE,{"derivedFrom":makeQuery(id+"F4.opExtrude","CAP_EDGE",EDGE,{"disambiguationData":[OSD([sQuery(id+"F3.wireOp",EDGE,"E11.1.3.0")])],"isStart":true}),"instanceName":"1"});
            var Q21;
            Q21=makeQuery(id+"F5.opPattern","COPY",EDGE,{"derivedFrom":makeQuery(id+"F4.opExtrude","CAP_EDGE",EDGE,{"disambiguationData":[OSD([sQuery(id+"F3.wireOp",EDGE,"E11.1.3.3")])],"isStart":true}),"instanceName":"1"});
            var Q22;
            Q22=makeQuery(id+"F5.opPattern","COPY",EDGE,{"derivedFrom":makeQuery(id+"F4.opExtrude","CAP_EDGE",EDGE,{"disambiguationData":[OSD([sQuery(id+"F3.wireOp",EDGE,"E11.0.2.0")])],"isStart":true}),"instanceName":"1"});
            var Q23;
            Q23=makeQuery(id+"F5.opPattern","COPY",EDGE,{"derivedFrom":makeQuery(id+"F4.opExtrude","CAP_EDGE",EDGE,{"disambiguationData":[OSD([sQuery(id+"F3.wireOp",EDGE,"E11.0.2.3")])],"isStart":true}),"instanceName":"1"});
            var Q24;
            Q24=makeQuery(id+"F5.opPattern","COPY",EDGE,{"derivedFrom":makeQuery(id+"F4.opExtrude","CAP_EDGE",EDGE,{"disambiguationData":[OSD([sQuery(id+"F3.wireOp",EDGE,"E10.0")])],"isStart":true}),"instanceName":"1"});
            var Q25;
            Q25=makeQuery(id+"F5.opPattern","COPY",EDGE,{"derivedFrom":makeQuery(id+"F4.opExtrude","CAP_EDGE",EDGE,{"disambiguationData":[OSD([sQuery(id+"F3.wireOp",EDGE,"E10.3")])],"isStart":true}),"instanceName":"1"});
            var Q26;
            Q26=makeQuery(id+"F5.opPattern","COPY",EDGE,{"derivedFrom":makeQuery(id+"F4.opExtrude","CAP_EDGE",EDGE,{"disambiguationData":[OSD([sQuery(id+"F3.wireOp",EDGE,"E10.2")])],"isStart":true}),"instanceName":"1"});
            var Q27;
            Q27=makeQuery(id+"F5.opPattern","COPY",EDGE,{"derivedFrom":makeQuery(id+"F4.opExtrude","CAP_EDGE",EDGE,{"disambiguationData":[OSD([sQuery(id+"F3.wireOp",EDGE,"E11.1.0.3")])],"isStart":true}),"instanceName":"1"});
            var Q28;
            Q28=makeQuery(id+"F5.opPattern","COPY",EDGE,{"derivedFrom":makeQuery(id+"F4.opExtrude","CAP_EDGE",EDGE,{"disambiguationData":[OSD([sQuery(id+"F3.wireOp",EDGE,"E11.1.0.2")])],"isStart":true}),"instanceName":"1"});
            var Q29;
            Q29=makeQuery(id+"F4.opExtrude","CAP_EDGE",EDGE,{"disambiguationData":[OSD([sQuery(id+"F3.wireOp",EDGE,"E11.1.0.2")])],"isStart":true});
            var Q30;
            Q30=makeQuery(id+"F4.opExtrude","CAP_EDGE",EDGE,{"disambiguationData":[OSD([sQuery(id+"F3.wireOp",EDGE,"E11.0.2.2")])],"isStart":true});
            var Q31;
            Q31=makeQuery(id+"F4.opExtrude","CAP_EDGE",EDGE,{"disambiguationData":[OSD([sQuery(id+"F3.wireOp",EDGE,"E11.2.1.2")])],"isStart":true});
            var Q32;
            Q32=makeQuery(id+"F4.opExtrude","CAP_EDGE",EDGE,{"disambiguationData":[OSD([sQuery(id+"F3.wireOp",EDGE,"E10.2")])],"isStart":true});
            var Q33;
            Q33=makeQuery(id+"F4.opExtrude","CAP_EDGE",EDGE,{"disambiguationData":[OSD([sQuery(id+"F3.wireOp",EDGE,"E11.1.3.2")])],"isStart":true});
            var Q34;
            Q34=makeQuery(id+"F4.opExtrude","CAP_EDGE",EDGE,{"disambiguationData":[OSD([sQuery(id+"F3.wireOp",EDGE,"E11.1.2.2")])],"isStart":true});
            var Q35;
            Q35=makeQuery(id+"F4.opExtrude","CAP_EDGE",EDGE,{"disambiguationData":[OSD([sQuery(id+"F3.wireOp",EDGE,"E11.2.2.2")])],"isStart":true});
            var Q36;
            Q36=makeQuery(id+"F5.opPattern","COPY",EDGE,{"derivedFrom":makeQuery(id+"F4.opExtrude","CAP_EDGE",EDGE,{"disambiguationData":[OSD([sQuery(id+"F3.wireOp",EDGE,"E11.1.0.1")])],"isStart":true}),"instanceName":"1"});
            var Q37;
            Q37=makeQuery(id+"F5.opPattern","COPY",EDGE,{"derivedFrom":makeQuery(id+"F4.opExtrude","CAP_EDGE",EDGE,{"disambiguationData":[OSD([sQuery(id+"F3.wireOp",EDGE,"E11.1.1.1")])],"isStart":true}),"instanceName":"1"});
            var Q38;
            Q38=makeQuery(id+"F5.opPattern","COPY",EDGE,{"derivedFrom":makeQuery(id+"F4.opExtrude","CAP_EDGE",EDGE,{"disambiguationData":[OSD([sQuery(id+"F3.wireOp",EDGE,"E11.1.1.2")])],"isStart":true}),"instanceName":"1"});
            var Q39;
            Q39=makeQuery(id+"F5.opPattern","COPY",EDGE,{"derivedFrom":makeQuery(id+"F4.opExtrude","CAP_EDGE",EDGE,{"disambiguationData":[OSD([sQuery(id+"F3.wireOp",EDGE,"E11.2.1.2")])],"isStart":true}),"instanceName":"1"});
            var Q40;
            Q40=makeQuery(id+"F5.opPattern","COPY",EDGE,{"derivedFrom":makeQuery(id+"F4.opExtrude","CAP_EDGE",EDGE,{"disambiguationData":[OSD([sQuery(id+"F3.wireOp",EDGE,"E11.2.1.1")])],"isStart":true}),"instanceName":"1"});
            var Q41;
            Q41=makeQuery(id+"F4.opExtrude","CAP_EDGE",EDGE,{"disambiguationData":[OSD([sQuery(id+"F3.wireOp",EDGE,"E11.1.0.1")])],"isStart":true});
            var Q42;
            Q42=makeQuery(id+"F4.opExtrude","CAP_EDGE",EDGE,{"disambiguationData":[OSD([sQuery(id+"F3.wireOp",EDGE,"E11.2.1.1")])],"isStart":true});
            var Q43;
            Q43=makeQuery(id+"F4.opExtrude","CAP_EDGE",EDGE,{"disambiguationData":[OSD([sQuery(id+"F3.wireOp",EDGE,"E11.2.2.1")])],"isStart":true});
            var Q44;
            Q44=makeQuery(id+"F4.opExtrude","CAP_EDGE",EDGE,{"disambiguationData":[OSD([sQuery(id+"F3.wireOp",EDGE,"E11.1.1.2")])],"isStart":true});
            var Q45;
            Q45=makeQuery(id+"F4.opExtrude","CAP_EDGE",EDGE,{"disambiguationData":[OSD([sQuery(id+"F3.wireOp",EDGE,"E11.1.1.1")])],"isStart":true});
            var Q46;
            Q46=makeQuery(id+"F4.opExtrude","CAP_EDGE",EDGE,{"disambiguationData":[OSD([sQuery(id+"F3.wireOp",EDGE,"E11.1.2.1")])],"isStart":true});
            var Q47;
            Q47=makeQuery(id+"F4.opExtrude","CAP_EDGE",EDGE,{"disambiguationData":[OSD([sQuery(id+"F3.wireOp",EDGE,"E10.1")])],"isStart":true});
            var Q48;
            Q48=makeQuery(id+"F4.opExtrude","CAP_EDGE",EDGE,{"disambiguationData":[OSD([sQuery(id+"F3.wireOp",EDGE,"E11.0.2.1")])],"isStart":true});
            var Q49;
            Q49=makeQuery(id+"F4.opExtrude","CAP_EDGE",EDGE,{"disambiguationData":[OSD([sQuery(id+"F3.wireOp",EDGE,"E11.1.3.1")])],"isStart":true});
            var Q50;
            Q50=makeQuery(id+"F4.opExtrude","CAP_EDGE",EDGE,{"disambiguationData":[OSD([sQuery(id+"F3.wireOp",EDGE,"E11.3.3.1")])],"isStart":true});
            var Q51;
            Q51=makeQuery(id+"F4.opExtrude","CAP_EDGE",EDGE,{"disambiguationData":[OSD([sQuery(id+"F3.wireOp",EDGE,"E11.3.3.2")])],"isStart":true});
            var Q52;
            Q52=makeQuery(id+"F5.opPattern","COPY",EDGE,{"derivedFrom":makeQuery(id+"F4.opExtrude","CAP_EDGE",EDGE,{"disambiguationData":[OSD([sQuery(id+"F3.wireOp",EDGE,"E11.1.3.1")])],"isStart":true}),"instanceName":"1"});
            var Q53;
            Q53=makeQuery(id+"F5.opPattern","COPY",EDGE,{"derivedFrom":makeQuery(id+"F4.opExtrude","CAP_EDGE",EDGE,{"disambiguationData":[OSD([sQuery(id+"F3.wireOp",EDGE,"E11.1.3.2")])],"isStart":true}),"instanceName":"1"});
            var Q54;
            Q54=makeQuery(id+"F5.opPattern","COPY",EDGE,{"derivedFrom":makeQuery(id+"F4.opExtrude","CAP_EDGE",EDGE,{"disambiguationData":[OSD([sQuery(id+"F3.wireOp",EDGE,"E11.3.3.2")])],"isStart":true}),"instanceName":"1"});
            var Q55;
            Q55=makeQuery(id+"F5.opPattern","COPY",EDGE,{"derivedFrom":makeQuery(id+"F4.opExtrude","CAP_EDGE",EDGE,{"disambiguationData":[OSD([sQuery(id+"F3.wireOp",EDGE,"E11.3.3.1")])],"isStart":true}),"instanceName":"1"});
            var Q56;
            Q56=makeQuery(id+"F5.opPattern","COPY",EDGE,{"derivedFrom":makeQuery(id+"F4.opExtrude","CAP_EDGE",EDGE,{"disambiguationData":[OSD([sQuery(id+"F3.wireOp",EDGE,"E11.2.2.1")])],"isStart":true}),"instanceName":"1"});
            var Q57;
            Q57=makeQuery(id+"F5.opPattern","COPY",EDGE,{"derivedFrom":makeQuery(id+"F4.opExtrude","CAP_EDGE",EDGE,{"disambiguationData":[OSD([sQuery(id+"F3.wireOp",EDGE,"E11.2.2.0")])],"isStart":true}),"instanceName":"1"});
            var Q58;
            Q58=makeQuery(id+"F5.opPattern","COPY",EDGE,{"derivedFrom":makeQuery(id+"F4.opExtrude","CAP_EDGE",EDGE,{"disambiguationData":[OSD([sQuery(id+"F3.wireOp",EDGE,"E11.2.2.3")])],"isStart":true}),"instanceName":"1"});
            var Q59;
            Q59=makeQuery(id+"F5.opPattern","COPY",EDGE,{"derivedFrom":makeQuery(id+"F4.opExtrude","CAP_EDGE",EDGE,{"disambiguationData":[OSD([sQuery(id+"F3.wireOp",EDGE,"E11.2.2.2")])],"isStart":true}),"instanceName":"1"});
            var Q60;
            Q60=makeQuery(id+"F5.opPattern","COPY",EDGE,{"derivedFrom":makeQuery(id+"F4.opExtrude","CAP_EDGE",EDGE,{"disambiguationData":[OSD([sQuery(id+"F3.wireOp",EDGE,"E11.2.1.0")])],"isStart":true}),"instanceName":"1"});
            var Q61;
            Q61=makeQuery(id+"F5.opPattern","COPY",EDGE,{"derivedFrom":makeQuery(id+"F4.opExtrude","CAP_EDGE",EDGE,{"disambiguationData":[OSD([sQuery(id+"F3.wireOp",EDGE,"E11.1.0.0")])],"isStart":true}),"instanceName":"1"});
            var Q62;
            Q62=makeQuery(id+"F5.opPattern","COPY",EDGE,{"derivedFrom":makeQuery(id+"F4.opExtrude","CAP_EDGE",EDGE,{"disambiguationData":[OSD([sQuery(id+"F3.wireOp",EDGE,"E11.1.1.0")])],"isStart":true}),"instanceName":"1"});
            var Q63;
            Q63=makeQuery(id+"F5.opPattern","COPY",EDGE,{"derivedFrom":makeQuery(id+"F4.opExtrude","CAP_EDGE",EDGE,{"disambiguationData":[OSD([sQuery(id+"F3.wireOp",EDGE,"E11.1.2.1")])],"isStart":true}),"instanceName":"1"});
            var Q64;
            Q64=makeQuery(id+"F5.opPattern","COPY",EDGE,{"derivedFrom":makeQuery(id+"F4.opExtrude","CAP_EDGE",EDGE,{"disambiguationData":[OSD([sQuery(id+"F3.wireOp",EDGE,"E11.1.2.0")])],"isStart":true}),"instanceName":"1"});
            var Q65;
            Q65=makeQuery(id+"F5.opPattern","COPY",EDGE,{"derivedFrom":makeQuery(id+"F4.opExtrude","CAP_EDGE",EDGE,{"disambiguationData":[OSD([sQuery(id+"F3.wireOp",EDGE,"E11.2.1.3")])],"isStart":true}),"instanceName":"1"});
            var Q66;
            Q66=makeQuery(id+"F5.opPattern","COPY",EDGE,{"derivedFrom":makeQuery(id+"F4.opExtrude","CAP_EDGE",EDGE,{"disambiguationData":[OSD([sQuery(id+"F3.wireOp",EDGE,"E11.1.2.3")])],"isStart":true}),"instanceName":"1"});
            var Q67;
            Q67=makeQuery(id+"F5.opPattern","COPY",EDGE,{"derivedFrom":makeQuery(id+"F4.opExtrude","CAP_EDGE",EDGE,{"disambiguationData":[OSD([sQuery(id+"F3.wireOp",EDGE,"E11.1.1.3")])],"isStart":true}),"instanceName":"1"});
            var Q68;
            Q68=makeQuery(id+"F5.opPattern","COPY",EDGE,{"derivedFrom":makeQuery(id+"F4.opExtrude","CAP_EDGE",EDGE,{"disambiguationData":[OSD([sQuery(id+"F3.wireOp",EDGE,"E11.1.2.2")])],"isStart":true}),"instanceName":"1"});
            var Q69;
            Q69=makeQuery(id+"F5.opPattern","COPY",EDGE,{"derivedFrom":makeQuery(id+"F4.opExtrude","CAP_EDGE",EDGE,{"disambiguationData":[OSD([sQuery(id+"F3.wireOp",EDGE,"E10.1")])],"isStart":true}),"instanceName":"1"});
            var Q70;
            Q70=makeQuery(id+"F5.opPattern","COPY",EDGE,{"derivedFrom":makeQuery(id+"F4.opExtrude","CAP_EDGE",EDGE,{"disambiguationData":[OSD([sQuery(id+"F3.wireOp",EDGE,"E11.0.2.2")])],"isStart":true}),"instanceName":"1"});
            var Q71;
            Q71=makeQuery(id+"F5.opPattern","COPY",EDGE,{"derivedFrom":makeQuery(id+"F4.opExtrude","CAP_EDGE",EDGE,{"disambiguationData":[OSD([sQuery(id+"F3.wireOp",EDGE,"E11.0.2.1")])],"isStart":true}),"instanceName":"1"});
            chamfer(context, id + "F6", {"entities" : qUnion([Q0, Q1, Q2, Q3, Q4, Q5, Q6, Q7, Q8, Q9, Q10, Q11, Q12, Q13, Q14, Q15, Q16, Q17, Q18, Q19, Q20, Q21, Q22, Q23, Q24, Q25, Q26, Q27, Q28, Q29, Q30, Q31, Q32, Q33, Q34, Q35, Q36, Q37, Q38, Q39, Q40, Q41, Q42, Q43, Q44, Q45, Q46, Q47, Q48, Q49, Q50, Q51, Q52, Q53, Q54, Q55, Q56, Q57, Q58, Q59, Q60, Q61, Q62, Q63, Q64, Q65, Q66, Q67, Q68, Q69, Q70, Q71]), "width" : 0.5 * mm, "tangentPropagation" : true});
        }
        {
            var Q0;
            Q0=makeQuery(id+"F2.opExtrude","CAP_EDGE",EDGE,{"disambiguationData":[OSD([sQuery(id+"F0.wireOp",EDGE,"E2.bottom")])],"isStart":false});
            var Q1;
            Q1=makeQuery(id+"F2.opExtrude","CAP_EDGE",EDGE,{"disambiguationData":[OSD([sQuery(id+"F0.wireOp",EDGE,"E5.filletArc")])],"isStart":false});
            var Q2;
            Q2=makeQuery(id+"F2.opExtrude","CAP_EDGE",EDGE,{"disambiguationData":[OSD([sQuery(id+"F0.wireOp",EDGE,"E2.right")])],"isStart":false});
            var Q3;
            Q3=makeQuery(id+"F2.opExtrude","CAP_EDGE",EDGE,{"disambiguationData":[OSD([sQuery(id+"F0.wireOp",EDGE,"E4.filletArc")])],"isStart":false});
            var Q4;
            Q4=makeQuery(id+"F2.opExtrude","CAP_EDGE",EDGE,{"disambiguationData":[OSD([sQuery(id+"F0.wireOp",EDGE,"E3.filletArc")])],"isStart":false});
            var Q5;
            Q5=makeQuery(id+"F2.opExtrude","CAP_EDGE",EDGE,{"disambiguationData":[OSD([sQuery(id+"F0.wireOp",EDGE,"E6.filletArc")])],"isStart":false});
            var Q6;
            Q6=makeQuery(id+"F2.opExtrude","CAP_EDGE",EDGE,{"disambiguationData":[OSD([sQuery(id+"F0.wireOp",EDGE,"E2.top")])],"isStart":false});
            var Q7;
            Q7=makeQuery(id+"F2.opExtrude","CAP_EDGE",EDGE,{"disambiguationData":[OSD([sQuery(id+"F0.wireOp",EDGE,"E2.left")])],"isStart":true});
            var Q8;
            Q8=makeQuery(id+"F2.opExtrude","CAP_EDGE",EDGE,{"disambiguationData":[OSD([sQuery(id+"F0.wireOp",EDGE,"E9")])],"isStart":false});
            var Q9;
            Q9=makeQuery(id+"F2.opExtrude","CAP_EDGE",EDGE,{"disambiguationData":[OSD([sQuery(id+"F0.wireOp",EDGE,"E9")])],"isStart":true});
            var Q10;
            Q10=makeQuery(id+"F5.opPattern","COPY",FACE,{"derivedFrom":makeQuery(id+"F4.opExtrude","CAP_FACE",FACE,{"disambiguationData":[OSD([sQuery(id+"F3.wireOp",EDGE,"E11.1.3.0"),sQuery(id+"F3.wireOp",EDGE,"E11.1.3.1"),sQuery(id+"F3.wireOp",EDGE,"E11.1.3.2"),sQuery(id+"F3.wireOp",EDGE,"E11.1.3.3")])],"isStart":false}),"instanceName":"1"});
            var Q11;
            Q11=makeQuery(id+"F5.opPattern","COPY",FACE,{"derivedFrom":makeQuery(id+"F4.opExtrude","CAP_FACE",FACE,{"disambiguationData":[OSD([sQuery(id+"F3.wireOp",EDGE,"E11.1.2.0"),sQuery(id+"F3.wireOp",EDGE,"E11.1.2.1"),sQuery(id+"F3.wireOp",EDGE,"E11.1.2.2"),sQuery(id+"F3.wireOp",EDGE,"E11.1.2.3")])],"isStart":false}),"instanceName":"1"});
            var Q12;
            Q12=makeQuery(id+"F5.opPattern","COPY",FACE,{"derivedFrom":makeQuery(id+"F4.opExtrude","CAP_FACE",FACE,{"disambiguationData":[OSD([sQuery(id+"F3.wireOp",EDGE,"E11.2.2.0"),sQuery(id+"F3.wireOp",EDGE,"E11.2.2.1"),sQuery(id+"F3.wireOp",EDGE,"E11.2.2.2"),sQuery(id+"F3.wireOp",EDGE,"E11.2.2.3")])],"isStart":false}),"instanceName":"1"});
            var Q13;
            Q13=makeQuery(id+"F5.opPattern","COPY",FACE,{"derivedFrom":makeQuery(id+"F4.opExtrude","CAP_FACE",FACE,{"disambiguationData":[OSD([sQuery(id+"F3.wireOp",EDGE,"E11.3.3.0"),sQuery(id+"F3.wireOp",EDGE,"E11.3.3.1"),sQuery(id+"F3.wireOp",EDGE,"E11.3.3.2"),sQuery(id+"F3.wireOp",EDGE,"E11.3.3.3")])],"isStart":false}),"instanceName":"1"});
            var Q14;
            Q14=makeQuery(id+"F5.opPattern","COPY",FACE,{"derivedFrom":makeQuery(id+"F4.opExtrude","CAP_FACE",FACE,{"disambiguationData":[OSD([sQuery(id+"F3.wireOp",EDGE,"E11.2.1.0"),sQuery(id+"F3.wireOp",EDGE,"E11.2.1.1"),sQuery(id+"F3.wireOp",EDGE,"E11.2.1.2"),sQuery(id+"F3.wireOp",EDGE,"E11.2.1.3")])],"isStart":false}),"instanceName":"1"});
            var Q15;
            Q15=makeQuery(id+"F5.opPattern","COPY",FACE,{"derivedFrom":makeQuery(id+"F4.opExtrude","CAP_FACE",FACE,{"disambiguationData":[OSD([sQuery(id+"F3.wireOp",EDGE,"E11.1.1.0"),sQuery(id+"F3.wireOp",EDGE,"E11.1.1.1"),sQuery(id+"F3.wireOp",EDGE,"E11.1.1.2"),sQuery(id+"F3.wireOp",EDGE,"E11.1.1.3")])],"isStart":false}),"instanceName":"1"});
            var Q16;
            Q16=makeQuery(id+"F5.opPattern","COPY",FACE,{"derivedFrom":makeQuery(id+"F4.opExtrude","CAP_FACE",FACE,{"disambiguationData":[OSD([sQuery(id+"F3.wireOp",EDGE,"E11.1.0.0"),sQuery(id+"F3.wireOp",EDGE,"E11.1.0.1"),sQuery(id+"F3.wireOp",EDGE,"E11.1.0.2"),sQuery(id+"F3.wireOp",EDGE,"E11.1.0.3")])],"isStart":false}),"instanceName":"1"});
            var Q17;
            Q17=makeQuery(id+"F5.opPattern","COPY",FACE,{"derivedFrom":makeQuery(id+"F4.opExtrude","CAP_FACE",FACE,{"disambiguationData":[OSD([sQuery(id+"F3.wireOp",EDGE,"E10.0"),sQuery(id+"F3.wireOp",EDGE,"E10.1"),sQuery(id+"F3.wireOp",EDGE,"E10.2"),sQuery(id+"F3.wireOp",EDGE,"E10.3")])],"isStart":false}),"instanceName":"1"});
            var Q18;
            Q18=makeQuery(id+"F5.opPattern","COPY",FACE,{"derivedFrom":makeQuery(id+"F4.opExtrude","CAP_FACE",FACE,{"disambiguationData":[OSD([sQuery(id+"F3.wireOp",EDGE,"E11.0.2.0"),sQuery(id+"F3.wireOp",EDGE,"E11.0.2.1"),sQuery(id+"F3.wireOp",EDGE,"E11.0.2.2"),sQuery(id+"F3.wireOp",EDGE,"E11.0.2.3")])],"isStart":false}),"instanceName":"1"});
            var Q19;
            Q19=makeQuery(id+"F4.opExtrude","CAP_FACE",FACE,{"disambiguationData":[OSD([sQuery(id+"F3.wireOp",EDGE,"E11.1.0.0"),sQuery(id+"F3.wireOp",EDGE,"E11.1.0.1"),sQuery(id+"F3.wireOp",EDGE,"E11.1.0.2"),sQuery(id+"F3.wireOp",EDGE,"E11.1.0.3")])],"isStart":false});
            var Q20;
            Q20=makeQuery(id+"F4.opExtrude","CAP_FACE",FACE,{"disambiguationData":[OSD([sQuery(id+"F3.wireOp",EDGE,"E10.0"),sQuery(id+"F3.wireOp",EDGE,"E10.1"),sQuery(id+"F3.wireOp",EDGE,"E10.2"),sQuery(id+"F3.wireOp",EDGE,"E10.3")])],"isStart":false});
            var Q21;
            Q21=makeQuery(id+"F4.opExtrude","CAP_FACE",FACE,{"disambiguationData":[OSD([sQuery(id+"F3.wireOp",EDGE,"E11.1.1.0"),sQuery(id+"F3.wireOp",EDGE,"E11.1.1.1"),sQuery(id+"F3.wireOp",EDGE,"E11.1.1.2"),sQuery(id+"F3.wireOp",EDGE,"E11.1.1.3")])],"isStart":false});
            var Q22;
            Q22=makeQuery(id+"F4.opExtrude","CAP_FACE",FACE,{"disambiguationData":[OSD([sQuery(id+"F3.wireOp",EDGE,"E11.2.1.0"),sQuery(id+"F3.wireOp",EDGE,"E11.2.1.1"),sQuery(id+"F3.wireOp",EDGE,"E11.2.1.2"),sQuery(id+"F3.wireOp",EDGE,"E11.2.1.3")])],"isStart":false});
            var Q23;
            Q23=makeQuery(id+"F4.opExtrude","CAP_FACE",FACE,{"disambiguationData":[OSD([sQuery(id+"F3.wireOp",EDGE,"E11.2.2.0"),sQuery(id+"F3.wireOp",EDGE,"E11.2.2.1"),sQuery(id+"F3.wireOp",EDGE,"E11.2.2.2"),sQuery(id+"F3.wireOp",EDGE,"E11.2.2.3")])],"isStart":false});
            var Q24;
            Q24=makeQuery(id+"F4.opExtrude","CAP_FACE",FACE,{"disambiguationData":[OSD([sQuery(id+"F3.wireOp",EDGE,"E11.3.3.0"),sQuery(id+"F3.wireOp",EDGE,"E11.3.3.1"),sQuery(id+"F3.wireOp",EDGE,"E11.3.3.2"),sQuery(id+"F3.wireOp",EDGE,"E11.3.3.3")])],"isStart":false});
            var Q25;
            Q25=makeQuery(id+"F4.opExtrude","CAP_FACE",FACE,{"disambiguationData":[OSD([sQuery(id+"F3.wireOp",EDGE,"E11.1.3.0"),sQuery(id+"F3.wireOp",EDGE,"E11.1.3.1"),sQuery(id+"F3.wireOp",EDGE,"E11.1.3.2"),sQuery(id+"F3.wireOp",EDGE,"E11.1.3.3")])],"isStart":false});
            var Q26;
            Q26=makeQuery(id+"F4.opExtrude","CAP_FACE",FACE,{"disambiguationData":[OSD([sQuery(id+"F3.wireOp",EDGE,"E11.0.2.0"),sQuery(id+"F3.wireOp",EDGE,"E11.0.2.1"),sQuery(id+"F3.wireOp",EDGE,"E11.0.2.2"),sQuery(id+"F3.wireOp",EDGE,"E11.0.2.3")])],"isStart":false});
            var Q27;
            Q27=makeQuery(id+"F4.opExtrude","CAP_FACE",FACE,{"disambiguationData":[OSD([sQuery(id+"F3.wireOp",EDGE,"E11.1.2.0"),sQuery(id+"F3.wireOp",EDGE,"E11.1.2.1"),sQuery(id+"F3.wireOp",EDGE,"E11.1.2.2"),sQuery(id+"F3.wireOp",EDGE,"E11.1.2.3")])],"isStart":false});
            fillet(context, id + "F7", {"entities" : qUnion([Q0, Q1, Q2, Q3, Q4, Q5, Q6, Q7, Q8, Q9, Q10, Q11, Q12, Q13, Q14, Q15, Q16, Q17, Q18, Q19, Q20, Q21, Q22, Q23, Q24, Q25, Q26, Q27]), "radius" : 1 * mm, "tangentPropagation" : true, "allowEdgeOverflow" : false});
        }
    });
